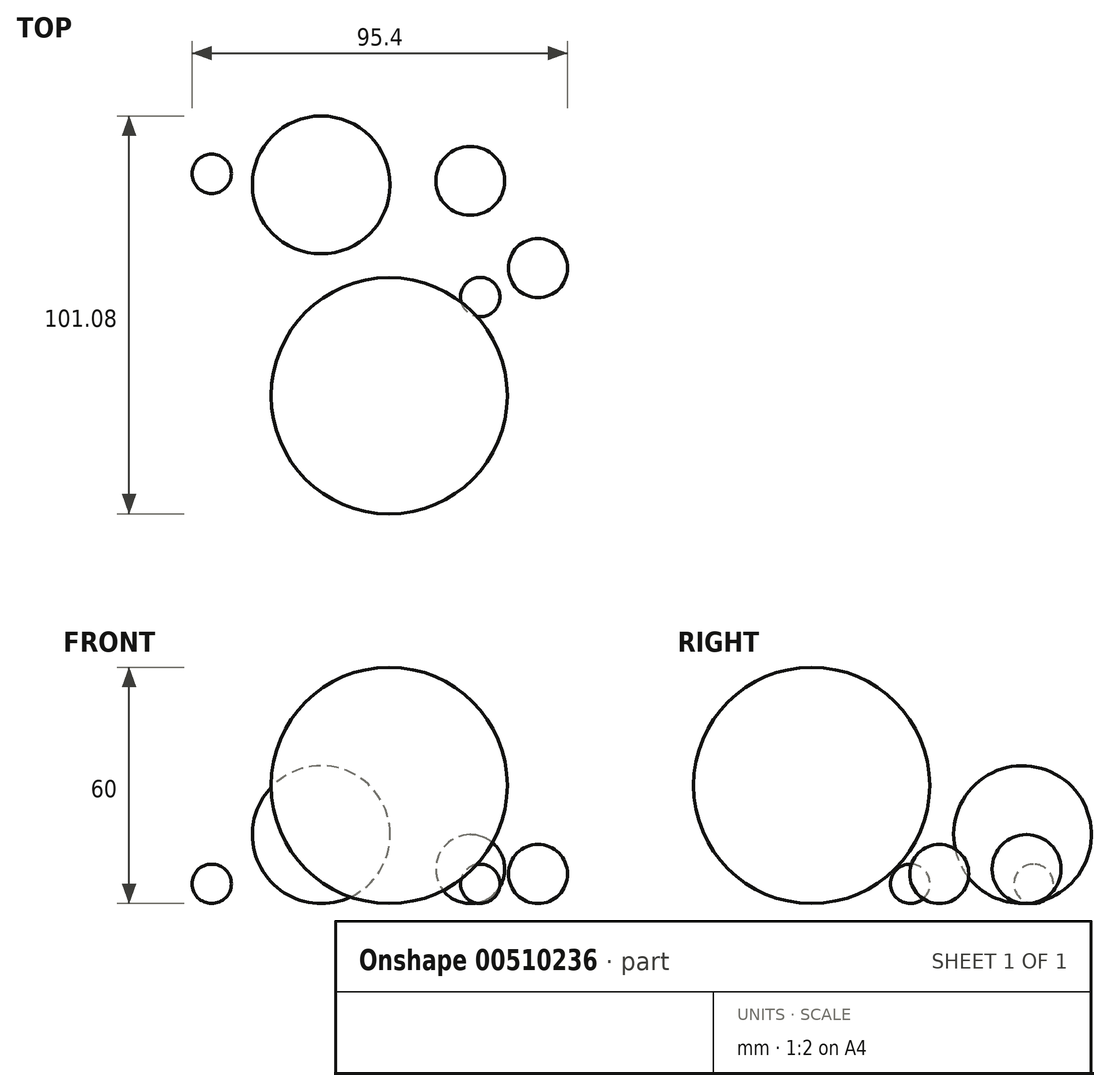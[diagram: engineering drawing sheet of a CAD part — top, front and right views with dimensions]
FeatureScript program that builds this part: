
annotation { "Feature Type Name" : "Feature", "Feature Type Description" : "" }
export const myFeature = defineFeature(function(context is Context, id is Id, definition is map)
    precondition{}
    {
        {
            var Q0;
            Q0=qCreatedBy(makeId("Top.planeOp"),FACE);
            var sketch = newSketch(context, id + "F0", { "sketchPlane" : qUnion([Q0])});
            skLineSegment(sketch, "E0.bottom", {"start": v(-30, 30) * mm, "end": v(30, 30) * mm});
            skLineSegment(sketch, "E0.top", {"start": v(-30, -30) * mm, "end": v(30, -30) * mm});
            skLineSegment(sketch, "E0.left", {"start": v(-30, 30) * mm, "end": v(-30, -30) * mm});
            skLineSegment(sketch, "E0.right", {"start": v(30, 30) * mm, "end": v(30, -30) * mm});
            skPoint(sketch, "E0.middle", {"position": v(0, 0) * mm});
            skSolve(sketch);
        }
        {
            var Q0;
            Q0=makeQuery(id+"F0.imprint","IMPRINT",FACE,{"disambiguationData":[TD([[makeQuery(id+"F0.imprint","IMPRINT",EDGE,{"derivedFrom":sQuery(id+"F0.wireOp",EDGE,"E0.bottom")}),-1.0]])]});
            extrude(context, id + "F1", {"entities" : qUnion([Q0]), "depth" : 60 * mm, "offsetDistance" : 25 * mm});
        }
        {
            var Q0;
            Q0=makeQuery(id+"F1.opExtrude","SWEPT_EDGE",EDGE,{"disambiguationData":[OSD([sQuery(id+"F0.wireOp",EDGE,"E0.top"),sQuery(id+"F0.wireOp",EDGE,"E0.right")])]});
            var Q1;
            Q1=makeQuery(id+"F1.opExtrude","SWEPT_FACE",FACE,{"disambiguationData":[OSD([sQuery(id+"F0.wireOp",EDGE,"E0.top")])]});
            var Q2;
            Q2=makeQuery(id+"F1.opExtrude","SWEPT_EDGE",EDGE,{"disambiguationData":[OSD([sQuery(id+"F0.wireOp",EDGE,"E0.top"),sQuery(id+"F0.wireOp",EDGE,"E0.left")])]});
            var Q3;
            Q3=makeQuery(id+"F1.opExtrude","CAP_FACE",FACE,{"disambiguationData":[OSD([sQuery(id+"F0.wireOp",EDGE,"E0.bottom"),sQuery(id+"F0.wireOp",EDGE,"E0.top"),sQuery(id+"F0.wireOp",EDGE,"E0.left"),sQuery(id+"F0.wireOp",EDGE,"E0.right")])],"isStart":true});
            var Q4;
            Q4=makeQuery(id+"F1.opExtrude","SWEPT_EDGE",EDGE,{"disambiguationData":[OSD([sQuery(id+"F0.wireOp",EDGE,"E0.bottom"),sQuery(id+"F0.wireOp",EDGE,"E0.right")])]});
            var Q5;
            Q5=makeQuery(id+"F1.opExtrude","SWEPT_FACE",FACE,{"disambiguationData":[OSD([sQuery(id+"F0.wireOp",EDGE,"E0.right")])]});
            var Q6;
            Q6=makeQuery(id+"F1.opExtrude","CAP_EDGE",EDGE,{"disambiguationData":[OSD([sQuery(id+"F0.wireOp",EDGE,"E0.top")])],"isStart":true});
            var Q7;
            Q7=makeQuery(id+"F1.opExtrude","CAP_EDGE",EDGE,{"disambiguationData":[OSD([sQuery(id+"F0.wireOp",EDGE,"E0.top")])],"isStart":false});
            var Q8;
            Q8=makeQuery(id+"F1.opExtrude","CAP_EDGE",EDGE,{"disambiguationData":[OSD([sQuery(id+"F0.wireOp",EDGE,"E0.right")])],"isStart":true});
            var Q9;
            Q9=makeQuery(id+"F1.opExtrude","CAP_EDGE",EDGE,{"disambiguationData":[OSD([sQuery(id+"F0.wireOp",EDGE,"E0.right")])],"isStart":false});
            var Q10;
            Q10=makeQuery(id+"F1.opExtrude","CAP_EDGE",EDGE,{"disambiguationData":[OSD([sQuery(id+"F0.wireOp",EDGE,"E0.bottom")])],"isStart":true});
            var Q11;
            Q11=makeQuery(id+"F1.opExtrude","CAP_EDGE",EDGE,{"disambiguationData":[OSD([sQuery(id+"F0.wireOp",EDGE,"E0.left")])],"isStart":true});
            var Q12;
            Q12=makeQuery(id+"F1.opExtrude","SWEPT_FACE",FACE,{"disambiguationData":[OSD([sQuery(id+"F0.wireOp",EDGE,"E0.bottom")])]});
            var Q13;
            Q13=makeQuery(id+"F1.opExtrude","SWEPT_EDGE",EDGE,{"disambiguationData":[OSD([sQuery(id+"F0.wireOp",EDGE,"E0.bottom"),sQuery(id+"F0.wireOp",EDGE,"E0.left")])]});
            var Q14;
            Q14=makeQuery(id+"F1.opExtrude","CAP_EDGE",EDGE,{"disambiguationData":[OSD([sQuery(id+"F0.wireOp",EDGE,"E0.bottom")])],"isStart":false});
            var Q15;
            Q15=makeQuery(id+"F1.opExtrude","CAP_FACE",FACE,{"disambiguationData":[OSD([sQuery(id+"F0.wireOp",EDGE,"E0.bottom"),sQuery(id+"F0.wireOp",EDGE,"E0.top"),sQuery(id+"F0.wireOp",EDGE,"E0.left"),sQuery(id+"F0.wireOp",EDGE,"E0.right")])],"isStart":false});
            var Q16;
            Q16=makeQuery(id+"F1.opExtrude","CAP_EDGE",EDGE,{"disambiguationData":[OSD([sQuery(id+"F0.wireOp",EDGE,"E0.left")])],"isStart":false});
            var Q17;
            Q17=makeQuery(id+"F1.opExtrude","SWEPT_FACE",FACE,{"disambiguationData":[OSD([sQuery(id+"F0.wireOp",EDGE,"E0.left")])]});
            fillet(context, id + "F2", {"entities" : qUnion([Q0, Q1, Q2, Q3, Q4, Q5, Q6, Q7, Q8, Q9, Q10, Q11, Q12, Q13, Q14, Q15, Q16, Q17]), "radius" : 30 * mm, "tangentPropagation" : true, "allowEdgeOverflow" : false});
        }
        {
            var Q0;
            Q0=qCreatedBy(makeId("Top.planeOp"),FACE);
            var sketch = newSketch(context, id + "F3", { "sketchPlane" : qUnion([Q0])});
            skLineSegment(sketch, "E1.bottom", {"start": v(18.12, 30.07) * mm, "end": v(28.12, 30.07) * mm});
            skLineSegment(sketch, "E1.top", {"start": v(18.12, 20.07) * mm, "end": v(28.12, 20.07) * mm});
            skLineSegment(sketch, "E1.left", {"start": v(18.12, 30.07) * mm, "end": v(18.12, 20.07) * mm});
            skLineSegment(sketch, "E1.right", {"start": v(28.12, 30.07) * mm, "end": v(28.12, 20.07) * mm});
            skSolve(sketch);
        }
        {
            var Q0;
            Q0=makeQuery(id+"F3.imprint","IMPRINT",FACE,{"disambiguationData":[TD([[makeQuery(id+"F3.imprint","IMPRINT",EDGE,{"derivedFrom":sQuery(id+"F3.wireOp",EDGE,"E1.bottom")}),-1.0]])]});
            extrude(context, id + "F4", {"entities" : qUnion([Q0]), "depth" : 10 * mm});
        }
        {
            var Q0;
            Q0=makeQuery(id+"F4.opExtrude","SWEPT_EDGE",EDGE,{"disambiguationData":[OSD([sQuery(id+"F3.wireOp",EDGE,"E1.bottom"),sQuery(id+"F3.wireOp",EDGE,"E1.right")])]});
            var Q1;
            Q1=makeQuery(id+"F4.opExtrude","SWEPT_EDGE",EDGE,{"disambiguationData":[OSD([sQuery(id+"F3.wireOp",EDGE,"E1.top"),sQuery(id+"F3.wireOp",EDGE,"E1.left")])]});
            var Q2;
            Q2=makeQuery(id+"F4.opExtrude","CAP_EDGE",EDGE,{"disambiguationData":[OSD([sQuery(id+"F3.wireOp",EDGE,"E1.right")])],"isStart":true});
            var Q3;
            Q3=makeQuery(id+"F4.opExtrude","CAP_EDGE",EDGE,{"disambiguationData":[OSD([sQuery(id+"F3.wireOp",EDGE,"E1.right")])],"isStart":false});
            var Q4;
            Q4=makeQuery(id+"F4.opExtrude","CAP_EDGE",EDGE,{"disambiguationData":[OSD([sQuery(id+"F3.wireOp",EDGE,"E1.top")])],"isStart":false});
            var Q5;
            Q5=makeQuery(id+"F4.opExtrude","CAP_EDGE",EDGE,{"disambiguationData":[OSD([sQuery(id+"F3.wireOp",EDGE,"E1.top")])],"isStart":true});
            var Q6;
            Q6=makeQuery(id+"F4.opExtrude","SWEPT_FACE",FACE,{"disambiguationData":[OSD([sQuery(id+"F3.wireOp",EDGE,"E1.right")])]});
            var Q7;
            Q7=makeQuery(id+"F4.opExtrude","SWEPT_FACE",FACE,{"disambiguationData":[OSD([sQuery(id+"F3.wireOp",EDGE,"E1.top")])]});
            var Q8;
            Q8=makeQuery(id+"F4.opExtrude","SWEPT_EDGE",EDGE,{"disambiguationData":[OSD([sQuery(id+"F3.wireOp",EDGE,"E1.top"),sQuery(id+"F3.wireOp",EDGE,"E1.right")])]});
            var Q9;
            Q9=makeQuery(id+"F4.opExtrude","CAP_FACE",FACE,{"disambiguationData":[OSD([sQuery(id+"F3.wireOp",EDGE,"E1.bottom"),sQuery(id+"F3.wireOp",EDGE,"E1.top"),sQuery(id+"F3.wireOp",EDGE,"E1.left"),sQuery(id+"F3.wireOp",EDGE,"E1.right")])],"isStart":true});
            var Q10;
            Q10=makeQuery(id+"F4.opExtrude","CAP_EDGE",EDGE,{"disambiguationData":[OSD([sQuery(id+"F3.wireOp",EDGE,"E1.left")])],"isStart":true});
            var Q11;
            Q11=makeQuery(id+"F4.opExtrude","CAP_EDGE",EDGE,{"disambiguationData":[OSD([sQuery(id+"F3.wireOp",EDGE,"E1.bottom")])],"isStart":true});
            var Q12;
            Q12=makeQuery(id+"F4.opExtrude","SWEPT_FACE",FACE,{"disambiguationData":[OSD([sQuery(id+"F3.wireOp",EDGE,"E1.bottom")])]});
            var Q13;
            Q13=makeQuery(id+"F4.opExtrude","SWEPT_FACE",FACE,{"disambiguationData":[OSD([sQuery(id+"F3.wireOp",EDGE,"E1.left")])]});
            var Q14;
            Q14=makeQuery(id+"F4.opExtrude","CAP_EDGE",EDGE,{"disambiguationData":[OSD([sQuery(id+"F3.wireOp",EDGE,"E1.bottom")])],"isStart":false});
            var Q15;
            Q15=makeQuery(id+"F4.opExtrude","CAP_EDGE",EDGE,{"disambiguationData":[OSD([sQuery(id+"F3.wireOp",EDGE,"E1.left")])],"isStart":false});
            var Q16;
            Q16=makeQuery(id+"F4.opExtrude","CAP_FACE",FACE,{"disambiguationData":[OSD([sQuery(id+"F3.wireOp",EDGE,"E1.bottom"),sQuery(id+"F3.wireOp",EDGE,"E1.top"),sQuery(id+"F3.wireOp",EDGE,"E1.left"),sQuery(id+"F3.wireOp",EDGE,"E1.right")])],"isStart":false});
            var Q17;
            Q17=makeQuery(id+"F4.opExtrude","SWEPT_EDGE",EDGE,{"disambiguationData":[OSD([sQuery(id+"F3.wireOp",EDGE,"E1.bottom"),sQuery(id+"F3.wireOp",EDGE,"E1.left")])]});
            fillet(context, id + "F5", {"entities" : qUnion([Q0, Q1, Q2, Q3, Q4, Q5, Q6, Q7, Q8, Q9, Q10, Q11, Q12, Q13, Q14, Q15, Q16, Q17]), "radius" : 5 * mm, "tangentPropagation" : true, "allowEdgeOverflow" : false});
        }
        {
            var Q0;
            Q0=qCreatedBy(makeId("Top.planeOp"),FACE);
            var sketch = newSketch(context, id + "F6", { "sketchPlane" : qUnion([Q0])});
            skLineSegment(sketch, "E2.bottom", {"start": v(30.31, 39.94) * mm, "end": v(45.31, 39.94) * mm});
            skLineSegment(sketch, "E2.top", {"start": v(30.31, 24.94) * mm, "end": v(45.31, 24.94) * mm});
            skLineSegment(sketch, "E2.left", {"start": v(30.31, 39.94) * mm, "end": v(30.31, 24.94) * mm});
            skLineSegment(sketch, "E2.right", {"start": v(45.31, 39.94) * mm, "end": v(45.31, 24.94) * mm});
            skSolve(sketch);
        }
        {
            var Q0;
            Q0=makeQuery(id+"F6.imprint","IMPRINT",FACE,{"disambiguationData":[TD([[makeQuery(id+"F6.imprint","IMPRINT",EDGE,{"derivedFrom":sQuery(id+"F6.wireOp",EDGE,"E2.bottom")}),-1.0]])]});
            extrude(context, id + "F7", {"entities" : qUnion([Q0]), "depth" : 15 * mm, "offsetDistance" : 25 * mm});
        }
        {
            var Q0;
            Q0=makeQuery(id+"F7.opExtrude","SWEPT_FACE",FACE,{"disambiguationData":[OSD([sQuery(id+"F6.wireOp",EDGE,"E2.right")])]});
            var Q1;
            Q1=makeQuery(id+"F7.opExtrude","CAP_EDGE",EDGE,{"disambiguationData":[OSD([sQuery(id+"F6.wireOp",EDGE,"E2.right")])],"isStart":true});
            var Q2;
            Q2=makeQuery(id+"F7.opExtrude","CAP_EDGE",EDGE,{"disambiguationData":[OSD([sQuery(id+"F6.wireOp",EDGE,"E2.right")])],"isStart":false});
            var Q3;
            Q3=makeQuery(id+"F7.opExtrude","CAP_EDGE",EDGE,{"disambiguationData":[OSD([sQuery(id+"F6.wireOp",EDGE,"E2.bottom")])],"isStart":false});
            var Q4;
            Q4=makeQuery(id+"F7.opExtrude","SWEPT_EDGE",EDGE,{"disambiguationData":[OSD([sQuery(id+"F6.wireOp",EDGE,"E2.top"),sQuery(id+"F6.wireOp",EDGE,"E2.right")])]});
            var Q5;
            Q5=makeQuery(id+"F7.opExtrude","SWEPT_EDGE",EDGE,{"disambiguationData":[OSD([sQuery(id+"F6.wireOp",EDGE,"E2.bottom"),sQuery(id+"F6.wireOp",EDGE,"E2.right")])]});
            var Q6;
            Q6=makeQuery(id+"F7.opExtrude","SWEPT_FACE",FACE,{"disambiguationData":[OSD([sQuery(id+"F6.wireOp",EDGE,"E2.bottom")])]});
            var Q7;
            Q7=makeQuery(id+"F7.opExtrude","SWEPT_EDGE",EDGE,{"disambiguationData":[OSD([sQuery(id+"F6.wireOp",EDGE,"E2.bottom"),sQuery(id+"F6.wireOp",EDGE,"E2.left")])]});
            var Q8;
            Q8=makeQuery(id+"F7.opExtrude","CAP_EDGE",EDGE,{"disambiguationData":[OSD([sQuery(id+"F6.wireOp",EDGE,"E2.bottom")])],"isStart":true});
            var Q9;
            Q9=makeQuery(id+"F7.opExtrude","SWEPT_EDGE",EDGE,{"disambiguationData":[OSD([sQuery(id+"F6.wireOp",EDGE,"E2.top"),sQuery(id+"F6.wireOp",EDGE,"E2.left")])]});
            var Q10;
            Q10=makeQuery(id+"F7.opExtrude","CAP_EDGE",EDGE,{"disambiguationData":[OSD([sQuery(id+"F6.wireOp",EDGE,"E2.top")])],"isStart":false});
            var Q11;
            Q11=makeQuery(id+"F7.opExtrude","CAP_EDGE",EDGE,{"disambiguationData":[OSD([sQuery(id+"F6.wireOp",EDGE,"E2.top")])],"isStart":true});
            var Q12;
            Q12=makeQuery(id+"F7.opExtrude","SWEPT_FACE",FACE,{"disambiguationData":[OSD([sQuery(id+"F6.wireOp",EDGE,"E2.top")])]});
            var Q13;
            Q13=makeQuery(id+"F7.opExtrude","CAP_FACE",FACE,{"disambiguationData":[OSD([sQuery(id+"F6.wireOp",EDGE,"E2.bottom"),sQuery(id+"F6.wireOp",EDGE,"E2.top"),sQuery(id+"F6.wireOp",EDGE,"E2.left"),sQuery(id+"F6.wireOp",EDGE,"E2.right")])],"isStart":true});
            var Q14;
            Q14=makeQuery(id+"F7.opExtrude","CAP_EDGE",EDGE,{"disambiguationData":[OSD([sQuery(id+"F6.wireOp",EDGE,"E2.left")])],"isStart":true});
            var Q15;
            Q15=makeQuery(id+"F7.opExtrude","SWEPT_FACE",FACE,{"disambiguationData":[OSD([sQuery(id+"F6.wireOp",EDGE,"E2.left")])]});
            var Q16;
            Q16=makeQuery(id+"F7.opExtrude","CAP_FACE",FACE,{"disambiguationData":[OSD([sQuery(id+"F6.wireOp",EDGE,"E2.bottom"),sQuery(id+"F6.wireOp",EDGE,"E2.top"),sQuery(id+"F6.wireOp",EDGE,"E2.left"),sQuery(id+"F6.wireOp",EDGE,"E2.right")])],"isStart":false});
            var Q17;
            Q17=makeQuery(id+"F7.opExtrude","CAP_EDGE",EDGE,{"disambiguationData":[OSD([sQuery(id+"F6.wireOp",EDGE,"E2.left")])],"isStart":false});
            fillet(context, id + "F8", {"entities" : qUnion([Q0, Q1, Q2, Q3, Q4, Q5, Q6, Q7, Q8, Q9, Q10, Q11, Q12, Q13, Q14, Q15, Q16, Q17]), "radius" : 7.5 * mm, "tangentPropagation" : true, "allowEdgeOverflow" : false});
        }
        {
            var Q0;
            Q0=qCreatedBy(makeId("Top.planeOp"),FACE);
            var sketch = newSketch(context, id + "F9", { "sketchPlane" : qUnion([Q0])});
            skLineSegment(sketch, "E3.bottom", {"start": v(11.84, 63.35) * mm, "end": v(29.34, 63.35) * mm});
            skLineSegment(sketch, "E3.top", {"start": v(11.84, 45.85) * mm, "end": v(29.34, 45.85) * mm});
            skLineSegment(sketch, "E3.left", {"start": v(11.84, 63.35) * mm, "end": v(11.84, 45.85) * mm});
            skLineSegment(sketch, "E3.right", {"start": v(29.34, 63.35) * mm, "end": v(29.34, 45.85) * mm});
            skSolve(sketch);
        }
        {
            var Q0;
            Q0=makeQuery(id+"F9.imprint","IMPRINT",FACE,{"disambiguationData":[TD([[makeQuery(id+"F9.imprint","IMPRINT",EDGE,{"derivedFrom":sQuery(id+"F9.wireOp",EDGE,"E3.bottom")}),-1.0]])]});
            extrude(context, id + "F10", {"entities" : qUnion([Q0]), "depth" : 17.5 * mm, "offsetDistance" : 25 * mm});
        }
        {
            var Q0;
            Q0=makeQuery(id+"F10.opExtrude","CAP_EDGE",EDGE,{"disambiguationData":[OSD([sQuery(id+"F9.wireOp",EDGE,"E3.left")])],"isStart":true});
            var Q1;
            Q1=makeQuery(id+"F10.opExtrude","CAP_EDGE",EDGE,{"disambiguationData":[OSD([sQuery(id+"F9.wireOp",EDGE,"E3.bottom")])],"isStart":true});
            var Q2;
            Q2=makeQuery(id+"F10.opExtrude","SWEPT_EDGE",EDGE,{"disambiguationData":[OSD([sQuery(id+"F9.wireOp",EDGE,"E3.top"),sQuery(id+"F9.wireOp",EDGE,"E3.left")])]});
            var Q3;
            Q3=makeQuery(id+"F10.opExtrude","SWEPT_EDGE",EDGE,{"disambiguationData":[OSD([sQuery(id+"F9.wireOp",EDGE,"E3.bottom"),sQuery(id+"F9.wireOp",EDGE,"E3.right")])]});
            var Q4;
            Q4=makeQuery(id+"F10.opExtrude","CAP_EDGE",EDGE,{"disambiguationData":[OSD([sQuery(id+"F9.wireOp",EDGE,"E3.right")])],"isStart":false});
            var Q5;
            Q5=makeQuery(id+"F10.opExtrude","CAP_EDGE",EDGE,{"disambiguationData":[OSD([sQuery(id+"F9.wireOp",EDGE,"E3.top")])],"isStart":false});
            var Q6;
            Q6=makeQuery(id+"F10.opExtrude","SWEPT_EDGE",EDGE,{"disambiguationData":[OSD([sQuery(id+"F9.wireOp",EDGE,"E3.bottom"),sQuery(id+"F9.wireOp",EDGE,"E3.left")])]});
            var Q7;
            Q7=makeQuery(id+"F10.opExtrude","SWEPT_FACE",FACE,{"disambiguationData":[OSD([sQuery(id+"F9.wireOp",EDGE,"E3.left")])]});
            var Q8;
            Q8=makeQuery(id+"F10.opExtrude","SWEPT_FACE",FACE,{"disambiguationData":[OSD([sQuery(id+"F9.wireOp",EDGE,"E3.top")])]});
            var Q9;
            Q9=makeQuery(id+"F10.opExtrude","SWEPT_EDGE",EDGE,{"disambiguationData":[OSD([sQuery(id+"F9.wireOp",EDGE,"E3.top"),sQuery(id+"F9.wireOp",EDGE,"E3.right")])]});
            var Q10;
            Q10=makeQuery(id+"F10.opExtrude","CAP_FACE",FACE,{"disambiguationData":[OSD([sQuery(id+"F9.wireOp",EDGE,"E3.bottom"),sQuery(id+"F9.wireOp",EDGE,"E3.top"),sQuery(id+"F9.wireOp",EDGE,"E3.left"),sQuery(id+"F9.wireOp",EDGE,"E3.right")])],"isStart":false});
            var Q11;
            Q11=makeQuery(id+"F10.opExtrude","SWEPT_FACE",FACE,{"disambiguationData":[OSD([sQuery(id+"F9.wireOp",EDGE,"E3.bottom")])]});
            var Q12;
            Q12=makeQuery(id+"F10.opExtrude","CAP_EDGE",EDGE,{"disambiguationData":[OSD([sQuery(id+"F9.wireOp",EDGE,"E3.right")])],"isStart":true});
            var Q13;
            Q13=makeQuery(id+"F10.opExtrude","CAP_EDGE",EDGE,{"disambiguationData":[OSD([sQuery(id+"F9.wireOp",EDGE,"E3.left")])],"isStart":false});
            var Q14;
            Q14=makeQuery(id+"F10.opExtrude","SWEPT_FACE",FACE,{"disambiguationData":[OSD([sQuery(id+"F9.wireOp",EDGE,"E3.right")])]});
            var Q15;
            Q15=makeQuery(id+"F10.opExtrude","CAP_FACE",FACE,{"disambiguationData":[OSD([sQuery(id+"F9.wireOp",EDGE,"E3.bottom"),sQuery(id+"F9.wireOp",EDGE,"E3.top"),sQuery(id+"F9.wireOp",EDGE,"E3.left"),sQuery(id+"F9.wireOp",EDGE,"E3.right")])],"isStart":true});
            var Q16;
            Q16=makeQuery(id+"F10.opExtrude","CAP_EDGE",EDGE,{"disambiguationData":[OSD([sQuery(id+"F9.wireOp",EDGE,"E3.bottom")])],"isStart":false});
            var Q17;
            Q17=makeQuery(id+"F10.opExtrude","CAP_EDGE",EDGE,{"disambiguationData":[OSD([sQuery(id+"F9.wireOp",EDGE,"E3.top")])],"isStart":true});
            fillet(context, id + "F11", {"entities" : qUnion([Q0, Q1, Q2, Q3, Q4, Q5, Q6, Q7, Q8, Q9, Q10, Q11, Q12, Q13, Q14, Q15, Q16, Q17]), "radius" : 8.7 * mm, "tangentPropagation" : true, "allowEdgeOverflow" : false});
        }
        {
            var Q0;
            Q0=qCreatedBy(makeId("Top.planeOp"),FACE);
            var sketch = newSketch(context, id + "F12", { "sketchPlane" : qUnion([Q0])});
            skLineSegment(sketch, "E4.bottom", {"start": v(-34.77, 71.08) * mm, "end": v(0.23, 71.08) * mm});
            skLineSegment(sketch, "E4.top", {"start": v(-34.77, 36.08) * mm, "end": v(0.23, 36.08) * mm});
            skLineSegment(sketch, "E4.left", {"start": v(-34.77, 71.08) * mm, "end": v(-34.77, 36.08) * mm});
            skLineSegment(sketch, "E4.right", {"start": v(0.23, 71.08) * mm, "end": v(0.23, 36.08) * mm});
            skSolve(sketch);
        }
        {
            var Q0;
            Q0=makeQuery(id+"F12.imprint","IMPRINT",FACE,{"disambiguationData":[TD([[makeQuery(id+"F12.imprint","IMPRINT",EDGE,{"derivedFrom":sQuery(id+"F12.wireOp",EDGE,"E4.bottom")}),-1.0]])]});
            extrude(context, id + "F13", {"entities" : qUnion([Q0]), "depth" : 35 * mm, "offsetDistance" : 25 * mm});
        }
        {
            var Q0;
            Q0=makeQuery(id+"F13.opExtrude","CAP_EDGE",EDGE,{"disambiguationData":[OSD([sQuery(id+"F12.wireOp",EDGE,"E4.right")])],"isStart":false});
            var Q1;
            Q1=makeQuery(id+"F13.opExtrude","SWEPT_FACE",FACE,{"disambiguationData":[OSD([sQuery(id+"F12.wireOp",EDGE,"E4.right")])]});
            var Q2;
            Q2=makeQuery(id+"F13.opExtrude","CAP_EDGE",EDGE,{"disambiguationData":[OSD([sQuery(id+"F12.wireOp",EDGE,"E4.bottom")])],"isStart":false});
            var Q3;
            Q3=makeQuery(id+"F13.opExtrude","SWEPT_FACE",FACE,{"disambiguationData":[OSD([sQuery(id+"F12.wireOp",EDGE,"E4.top")])]});
            var Q4;
            Q4=makeQuery(id+"F13.opExtrude","CAP_FACE",FACE,{"disambiguationData":[OSD([sQuery(id+"F12.wireOp",EDGE,"E4.bottom"),sQuery(id+"F12.wireOp",EDGE,"E4.top"),sQuery(id+"F12.wireOp",EDGE,"E4.left"),sQuery(id+"F12.wireOp",EDGE,"E4.right")])],"isStart":false});
            var Q5;
            Q5=makeQuery(id+"F13.opExtrude","CAP_FACE",FACE,{"disambiguationData":[OSD([sQuery(id+"F12.wireOp",EDGE,"E4.bottom"),sQuery(id+"F12.wireOp",EDGE,"E4.top"),sQuery(id+"F12.wireOp",EDGE,"E4.left"),sQuery(id+"F12.wireOp",EDGE,"E4.right")])],"isStart":true});
            var Q6;
            Q6=makeQuery(id+"F13.opExtrude","SWEPT_FACE",FACE,{"disambiguationData":[OSD([sQuery(id+"F12.wireOp",EDGE,"E4.bottom")])]});
            var Q7;
            Q7=makeQuery(id+"F13.opExtrude","SWEPT_EDGE",EDGE,{"disambiguationData":[OSD([sQuery(id+"F12.wireOp",EDGE,"E4.top"),sQuery(id+"F12.wireOp",EDGE,"E4.right")])]});
            var Q8;
            Q8=makeQuery(id+"F13.opExtrude","CAP_EDGE",EDGE,{"disambiguationData":[OSD([sQuery(id+"F12.wireOp",EDGE,"E4.left")])],"isStart":false});
            var Q9;
            Q9=makeQuery(id+"F13.opExtrude","CAP_EDGE",EDGE,{"disambiguationData":[OSD([sQuery(id+"F12.wireOp",EDGE,"E4.right")])],"isStart":true});
            var Q10;
            Q10=makeQuery(id+"F13.opExtrude","CAP_EDGE",EDGE,{"disambiguationData":[OSD([sQuery(id+"F12.wireOp",EDGE,"E4.top")])],"isStart":false});
            var Q11;
            Q11=makeQuery(id+"F13.opExtrude","CAP_EDGE",EDGE,{"disambiguationData":[OSD([sQuery(id+"F12.wireOp",EDGE,"E4.top")])],"isStart":true});
            var Q12;
            Q12=makeQuery(id+"F13.opExtrude","SWEPT_FACE",FACE,{"disambiguationData":[OSD([sQuery(id+"F12.wireOp",EDGE,"E4.left")])]});
            var Q13;
            Q13=makeQuery(id+"F13.opExtrude","CAP_EDGE",EDGE,{"disambiguationData":[OSD([sQuery(id+"F12.wireOp",EDGE,"E4.bottom")])],"isStart":true});
            var Q14;
            Q14=makeQuery(id+"F13.opExtrude","SWEPT_EDGE",EDGE,{"disambiguationData":[OSD([sQuery(id+"F12.wireOp",EDGE,"E4.bottom"),sQuery(id+"F12.wireOp",EDGE,"E4.left")])]});
            var Q15;
            Q15=makeQuery(id+"F13.opExtrude","CAP_EDGE",EDGE,{"disambiguationData":[OSD([sQuery(id+"F12.wireOp",EDGE,"E4.left")])],"isStart":true});
            fillet(context, id + "F14", {"entities" : qUnion([Q0, Q1, Q2, Q3, Q4, Q5, Q6, Q7, Q8, Q9, Q10, Q11, Q12, Q13, Q14, Q15]), "radius" : 17.5 * mm, "tangentPropagation" : true, "allowEdgeOverflow" : false});
        }
        {
            var Q0;
            Q0=qCreatedBy(makeId("Top.planeOp"),FACE);
            var sketch = newSketch(context, id + "F15", { "sketchPlane" : qUnion([Q0])});
            skLineSegment(sketch, "E5.bottom", {"start": v(-50.1, 61.4) * mm, "end": v(-40.1, 61.4) * mm});
            skLineSegment(sketch, "E5.top", {"start": v(-50.1, 51.4) * mm, "end": v(-40.1, 51.4) * mm});
            skLineSegment(sketch, "E5.left", {"start": v(-50.1, 61.4) * mm, "end": v(-50.1, 51.4) * mm});
            skLineSegment(sketch, "E5.right", {"start": v(-40.1, 61.4) * mm, "end": v(-40.1, 51.4) * mm});
            skSolve(sketch);
        }
        {
            var Q0;
            Q0=makeQuery(id+"F15.imprint","IMPRINT",FACE,{"disambiguationData":[TD([[makeQuery(id+"F15.imprint","IMPRINT",EDGE,{"derivedFrom":sQuery(id+"F15.wireOp",EDGE,"E5.bottom")}),-1.0]])]});
            extrude(context, id + "F16", {"entities" : qUnion([Q0]), "depth" : 10 * mm, "offsetDistance" : 25 * mm});
        }
        {
            var Q0;
            Q0=makeQuery(id+"F16.opExtrude","CAP_FACE",FACE,{"disambiguationData":[OSD([sQuery(id+"F15.wireOp",EDGE,"E5.bottom"),sQuery(id+"F15.wireOp",EDGE,"E5.top"),sQuery(id+"F15.wireOp",EDGE,"E5.left"),sQuery(id+"F15.wireOp",EDGE,"E5.right")])],"isStart":false});
            var Q1;
            Q1=makeQuery(id+"F16.opExtrude","SWEPT_EDGE",EDGE,{"disambiguationData":[OSD([sQuery(id+"F15.wireOp",EDGE,"E5.top"),sQuery(id+"F15.wireOp",EDGE,"E5.left")])]});
            var Q2;
            Q2=makeQuery(id+"F16.opExtrude","CAP_FACE",FACE,{"disambiguationData":[OSD([sQuery(id+"F15.wireOp",EDGE,"E5.bottom"),sQuery(id+"F15.wireOp",EDGE,"E5.top"),sQuery(id+"F15.wireOp",EDGE,"E5.left"),sQuery(id+"F15.wireOp",EDGE,"E5.right")])],"isStart":true});
            var Q3;
            Q3=makeQuery(id+"F16.opExtrude","SWEPT_FACE",FACE,{"disambiguationData":[OSD([sQuery(id+"F15.wireOp",EDGE,"E5.bottom")])]});
            var Q4;
            Q4=makeQuery(id+"F16.opExtrude","SWEPT_EDGE",EDGE,{"disambiguationData":[OSD([sQuery(id+"F15.wireOp",EDGE,"E5.bottom"),sQuery(id+"F15.wireOp",EDGE,"E5.right")])]});
            var Q5;
            Q5=makeQuery(id+"F16.opExtrude","SWEPT_FACE",FACE,{"disambiguationData":[OSD([sQuery(id+"F15.wireOp",EDGE,"E5.left")])]});
            var Q6;
            Q6=makeQuery(id+"F16.opExtrude","SWEPT_EDGE",EDGE,{"disambiguationData":[OSD([sQuery(id+"F15.wireOp",EDGE,"E5.bottom"),sQuery(id+"F15.wireOp",EDGE,"E5.left")])]});
            var Q7;
            Q7=makeQuery(id+"F16.opExtrude","SWEPT_FACE",FACE,{"disambiguationData":[OSD([sQuery(id+"F15.wireOp",EDGE,"E5.top")])]});
            var Q8;
            Q8=makeQuery(id+"F16.opExtrude","CAP_EDGE",EDGE,{"disambiguationData":[OSD([sQuery(id+"F15.wireOp",EDGE,"E5.left")])],"isStart":false});
            var Q9;
            Q9=makeQuery(id+"F16.opExtrude","CAP_EDGE",EDGE,{"disambiguationData":[OSD([sQuery(id+"F15.wireOp",EDGE,"E5.top")])],"isStart":true});
            var Q10;
            Q10=makeQuery(id+"F16.opExtrude","CAP_EDGE",EDGE,{"disambiguationData":[OSD([sQuery(id+"F15.wireOp",EDGE,"E5.top")])],"isStart":false});
            var Q11;
            Q11=makeQuery(id+"F16.opExtrude","CAP_EDGE",EDGE,{"disambiguationData":[OSD([sQuery(id+"F15.wireOp",EDGE,"E5.left")])],"isStart":true});
            var Q12;
            Q12=makeQuery(id+"F16.opExtrude","CAP_EDGE",EDGE,{"disambiguationData":[OSD([sQuery(id+"F15.wireOp",EDGE,"E5.bottom")])],"isStart":true});
            var Q13;
            Q13=makeQuery(id+"F16.opExtrude","SWEPT_FACE",FACE,{"disambiguationData":[OSD([sQuery(id+"F15.wireOp",EDGE,"E5.right")])]});
            var Q14;
            Q14=makeQuery(id+"F16.opExtrude","CAP_EDGE",EDGE,{"disambiguationData":[OSD([sQuery(id+"F15.wireOp",EDGE,"E5.bottom")])],"isStart":false});
            var Q15;
            Q15=makeQuery(id+"F16.opExtrude","SWEPT_EDGE",EDGE,{"disambiguationData":[OSD([sQuery(id+"F15.wireOp",EDGE,"E5.top"),sQuery(id+"F15.wireOp",EDGE,"E5.right")])]});
            var Q16;
            Q16=makeQuery(id+"F16.opExtrude","CAP_EDGE",EDGE,{"disambiguationData":[OSD([sQuery(id+"F15.wireOp",EDGE,"E5.right")])],"isStart":false});
            var Q17;
            Q17=makeQuery(id+"F16.opExtrude","CAP_EDGE",EDGE,{"disambiguationData":[OSD([sQuery(id+"F15.wireOp",EDGE,"E5.right")])],"isStart":true});
            fillet(context, id + "F17", {"entities" : qUnion([Q0, Q1, Q2, Q3, Q4, Q5, Q6, Q7, Q8, Q9, Q10, Q11, Q12, Q13, Q14, Q15, Q16, Q17]), "radius" : 5 * mm, "tangentPropagation" : true, "allowEdgeOverflow" : false});
        }
    });
